annotation { "Feature Type Name" : "Feature", "Feature Type Description" : "" }
export const myFeature = defineFeature(function(context is Context, id is Id, definition is map)
    precondition{}
    {
        {
            var Q0;
            Q0=qCreatedBy(makeId("Top.planeOp"),FACE);
            var sketch = newSketch(context, id + "F0", { "sketchPlane" : qUnion([Q0])});
            skLineSegment(sketch, "E0", {"start": v(-5.5, 76.5) * mm, "end": v(-69, -33.49) * mm});
            skLineSegment(sketch, "E1", {"start": v(-63.5, -43.01) * mm, "end": v(63.5, -43.01) * mm});
            skLineSegment(sketch, "E2", {"start": v(69, -33.49) * mm, "end": v(5.5, 76.5) * mm});
            skPoint(sketch, "E3.visualSharp", {"position": v(0, 86.02) * mm});
            skArc(sketch, "E3.filletArc", {"start": v(5.5, 76.5) * mm, "mid": v(0, 79.67) * mm, "end": v(-5.5, 76.5) * mm});
            skPoint(sketch, "E4.visualSharp", {"position": v(-74.5, -43.01) * mm});
            skArc(sketch, "E4.filletArc", {"start": v(-69, -33.49) * mm, "mid": v(-69, -39.84) * mm, "end": v(-63.5, -43.01) * mm});
            skPoint(sketch, "E5.visualSharp", {"position": v(74.5, -43.01) * mm});
            skArc(sketch, "E5.filletArc", {"start": v(63.5, -43.01) * mm, "mid": v(69, -39.84) * mm, "end": v(69, -33.49) * mm});
            skLineSegment(sketch, "E6", {"start": v(0, 73.32) * mm, "end": v(0, 0) * mm, "construction": true});
            skPoint(sketch, "E6.endSnap0", {"position": v(0, -43.01) * mm});
            skLineSegment(sketch, "E7", {"start": v(0, 0) * mm, "end": v(-63.5, -36.66) * mm, "construction": true});
            skLineSegment(sketch, "E8", {"start": v(0, 0) * mm, "end": v(63.5, -36.66) * mm, "construction": true});
            skArc(sketch, "E9", {"start": v(4.83, -4.76) * mm, "mid": v(9.52, 0.03) * mm, "end": v(4.76, 4.76) * mm});
            skArc(sketch, "E10", {"start": v(-4.75, 4.76) * mm, "mid": v(-9.52, 0) * mm, "end": v(-4.76, -4.76) * mm});
            skLineSegment(sketch, "E11", {"start": v(4.76, 0) * mm, "end": v(-4.76, 0) * mm, "construction": true});
            skLineSegment(sketch, "E12", {"start": v(-4.75, 4.76) * mm, "end": v(4.76, 4.76) * mm});
            skLineSegment(sketch, "E13", {"start": v(4.83, -4.76) * mm, "end": v(-4.76, -4.76) * mm});
            skSolve(sketch);
        }
        {
            var Q0;
            Q0 = qSketchRegion(id + "F0", true);
            extrude(context, id + "F1", {"entities" : qUnion([Q0]), "depth" : 2.54 * mm});
        }
        {
            var Q0;
            Q0=makeQuery(id+"F1.opExtrude","CAP_FACE",FACE,{"disambiguationData":[OSD([sQuery(id+"F0.wireOp",EDGE,"E0"),sQuery(id+"F0.wireOp",EDGE,"E1"),sQuery(id+"F0.wireOp",EDGE,"E2"),sQuery(id+"F0.wireOp",EDGE,"E3.filletArc"),sQuery(id+"F0.wireOp",EDGE,"E4.filletArc"),sQuery(id+"F0.wireOp",EDGE,"E5.filletArc"),sQuery(id+"F0.wireOp",EDGE,"E9"),sQuery(id+"F0.wireOp",EDGE,"E10"),sQuery(id+"F0.wireOp",EDGE,"E12"),sQuery(id+"F0.wireOp",EDGE,"E13")])],"isStart":false});
            var sketch = newSketch(context, id + "F2", { "sketchPlane" : qUnion([Q0])});
            skLineSegment(sketch, "E14", {"start": v(-69, -33.49) * mm, "end": v(-5.5, 76.5) * mm});
            skLineSegment(sketch, "E15", {"start": v(5.5, 76.5) * mm, "end": v(69, -33.49) * mm});
            skLineSegment(sketch, "E16", {"start": v(63.5, -43.01) * mm, "end": v(-63.5, -43.01) * mm});
            skArc(sketch, "E17", {"start": v(-69, -33.49) * mm, "mid": v(-69, -39.84) * mm, "end": v(-63.5, -43.01) * mm});
            skArc(sketch, "E18", {"start": v(5.5, 76.5) * mm, "mid": v(0, 79.67) * mm, "end": v(-5.5, 76.5) * mm});
            skArc(sketch, "E19", {"start": v(63.5, -43.01) * mm, "mid": v(69, -39.84) * mm, "end": v(69, -33.49) * mm});
            skArc(sketch, "E20.0", {"start": v(-66.36, -35.01) * mm, "mid": v(-66.36, -38.31) * mm, "end": v(-63.5, -39.96) * mm});
            skArc(sketch, "E20.1", {"start": v(2.86, 74.97) * mm, "mid": v(0, 76.62) * mm, "end": v(-2.86, 74.97) * mm});
            skLineSegment(sketch, "E20.2", {"start": v(2.86, 74.97) * mm, "end": v(66.36, -35.01) * mm});
            skLineSegment(sketch, "E20.3", {"start": v(-66.36, -35.01) * mm, "end": v(-2.86, 74.97) * mm});
            skArc(sketch, "E20.4", {"start": v(63.5, -39.96) * mm, "mid": v(66.36, -38.31) * mm, "end": v(66.36, -35.01) * mm});
            skLineSegment(sketch, "E20.5", {"start": v(63.5, -39.96) * mm, "end": v(-63.5, -39.96) * mm});
            skSolve(sketch);
        }
        {
            var Q0;
            Q0 = qSketchRegion(id + "F2", true);
            extrude(context, id + "F3", {"entities" : qUnion([Q0]), "operationType" : NewBodyOperationType.ADD, "depth" : 2.54 * mm});
        }
        {
            var Q0;
            Q0=makeQuery(id+"F1.opExtrude","CAP_FACE",FACE,{"disambiguationData":[OSD([sQuery(id+"F0.wireOp",EDGE,"E0"),sQuery(id+"F0.wireOp",EDGE,"E1"),sQuery(id+"F0.wireOp",EDGE,"E2"),sQuery(id+"F0.wireOp",EDGE,"E3.filletArc"),sQuery(id+"F0.wireOp",EDGE,"E4.filletArc"),sQuery(id+"F0.wireOp",EDGE,"E5.filletArc"),sQuery(id+"F0.wireOp",EDGE,"E9"),sQuery(id+"F0.wireOp",EDGE,"E10"),sQuery(id+"F0.wireOp",EDGE,"E12"),sQuery(id+"F0.wireOp",EDGE,"E13")])],"isStart":false});
            var sketch = newSketch(context, id + "F4", { "sketchPlane" : qUnion([Q0])});
            skText(sketch, "E21", { "text": "BEACH WESTERNS", "fontName": "OpenSans-Bold.ttf"});
            skText(sketch, "E22", { "text": "2016", "fontName": "OpenSans-Bold.ttf"});
            const initialGuessF4  = {"E21": [-0.05981, -0.03679, 1, 0, 0.00952], "E22": [-0.02137, -0.02271, 1, 0, 0.01314]};
            skSetInitialGuess(sketch, initialGuessF4);
            skSolve(sketch);
        }
        {
            var Q0;
            Q0 = qSketchRegion(id + "F4", true);
            extrude(context, id + "F5", {"entities" : qUnion([Q0]), "operationType" : NewBodyOperationType.ADD, "depth" : 1.52 * mm});
        }
    });